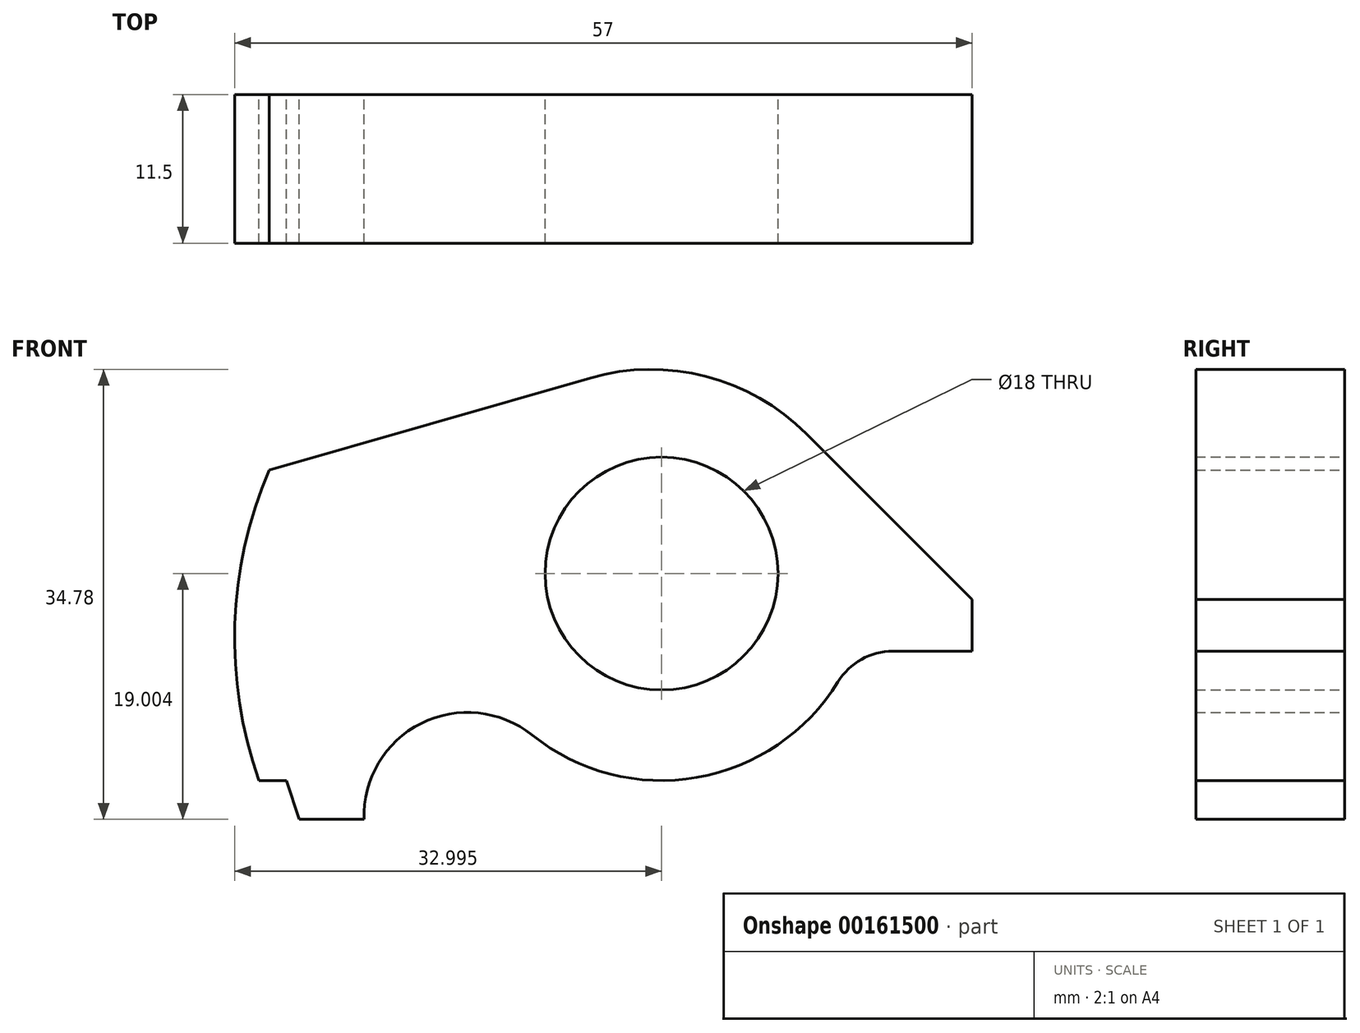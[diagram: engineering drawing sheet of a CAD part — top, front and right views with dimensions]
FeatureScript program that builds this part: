
annotation { "Feature Type Name" : "Feature", "Feature Type Description" : "" }
export const myFeature = defineFeature(function(context is Context, id is Id, definition is map)
    precondition{}
    {
        {
            var Q0;
            Q0=qCreatedBy(makeId("Front.planeOp"),FACE);
            var sketch = newSketch(context, id + "F0", { "sketchPlane" : qUnion([Q0])});
            skCircle(sketch, "E0", {"center": v(-45.03, 44.42) * mm, "radius": 9 * mm});
            skPoint(sketch, "E1", {"position": v(-45.03, 39.42) * mm});
            skLineSegment(sketch, "E2", {"start": v(-81.08, 44.42) * mm, "end": v(-2.9, 44.42) * mm, "construction": true});
            skLineSegment(sketch, "E3", {"start": v(-21.03, 42.42) * mm, "end": v(-21.03, 38.42) * mm});
            skLineSegment(sketch, "E4", {"start": v(-21.03, 42.42) * mm, "end": v(-33.83, 55.22) * mm});
            skArc(sketch, "E5", {"start": v(-55.03, 31.93) * mm, "mid": v(-42.3, 28.66) * mm, "end": v(-31.4, 36.04) * mm});
            skLineSegment(sketch, "E6", {"start": v(-76.15, 28.42) * mm, "end": v(-74.03, 28.42) * mm});
            skLineSegment(sketch, "E7", {"start": v(-74.03, 28.42) * mm, "end": v(-73.03, 25.42) * mm});
            skLineSegment(sketch, "E8", {"start": v(-21.03, 38.42) * mm, "end": v(-27.15, 38.42) * mm});
            skArc(sketch, "E9", {"start": v(-31.4, 36.04) * mm, "mid": v(-29.59, 37.79) * mm, "end": v(-27.15, 38.42) * mm});
            skPoint(sketch, "E10", {"position": v(-60.03, 25.69) * mm});
            skArc(sketch, "E11", {"start": v(-75.37, 52.42) * mm, "mid": v(-78.02, 40.5) * mm, "end": v(-76.15, 28.42) * mm});
            skPoint(sketch, "E12.orphan", {"position": v(-77.58, 51.9) * mm});
            skPoint(sketch, "E13.orphan", {"position": v(-78.87, 28.42) * mm});
            skArc(sketch, "E14", {"start": v(-55.03, 31.93) * mm, "mid": v(-63.62, 32.84) * mm, "end": v(-68.03, 25.42) * mm});
            skLineSegment(sketch, "E15", {"start": v(-73.03, 25.42) * mm, "end": v(-68.03, 25.42) * mm});
            skPoint(sketch, "E16.orphan", {"position": v(-57.09, 56.41) * mm});
            skLineSegment(sketch, "E17", {"start": v(-75.37, 52.42) * mm, "end": v(-50.54, 59.54) * mm});
            skArc(sketch, "E18", {"start": v(-50.54, 59.54) * mm, "mid": v(-41.6, 59.66) * mm, "end": v(-33.83, 55.22) * mm});
            skLineSegment(sketch, "E19", {"start": v(-74.03, 28.42) * mm, "end": v(-74.03, 18.81) * mm, "construction": true});
            skSolve(sketch);
        }
        {
            var Q0;
            Q0=makeQuery(id+"F0.imprint","IMPRINT",FACE,{"disambiguationData":[TD([[makeQuery(id+"F0.imprint","IMPRINT",EDGE,{"derivedFrom":sQuery(id+"F0.wireOp",EDGE,"E0")}),-1.0]])]});
            extrude(context, id + "F1", {"entities" : qUnion([Q0]), "depth" : 11.5 * mm});
        }
    });
